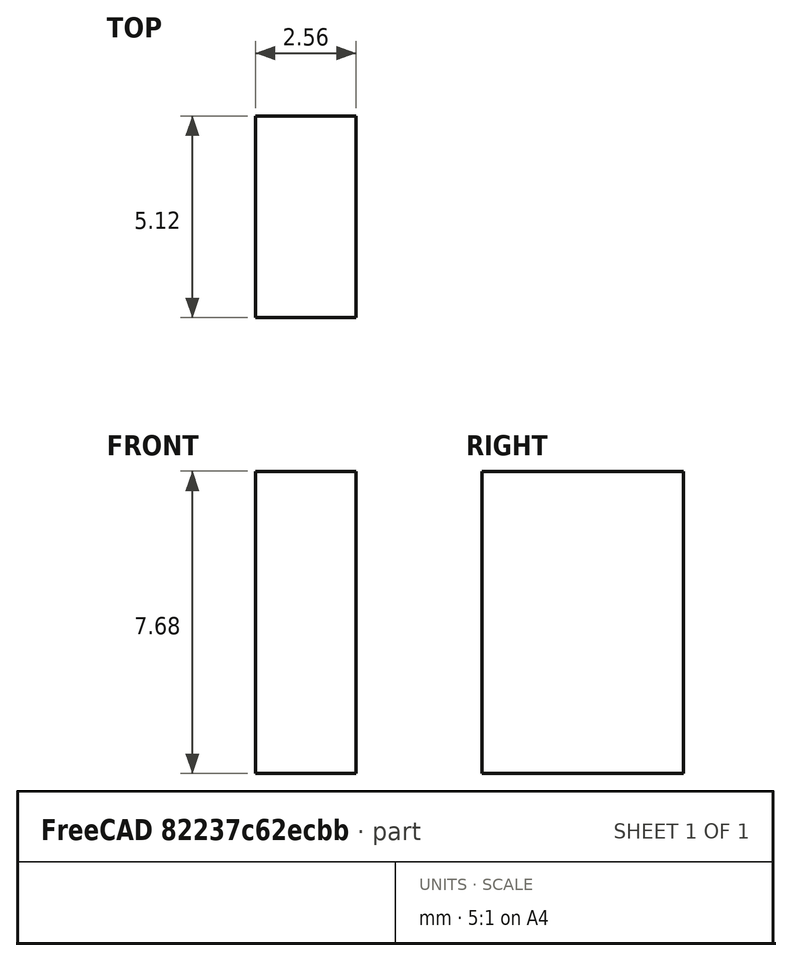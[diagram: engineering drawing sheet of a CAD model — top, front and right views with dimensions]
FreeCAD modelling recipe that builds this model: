
FCSTD DOCUMENT  (FreeCAD 0.19R)
Label: simple-ctrlr
License: All rights reserved
LicenseURL: http://en.wikipedia.org/wiki/All_rights_reserved
objects: App::FeaturePython×2, Part::Box×1, App::DocumentObjectGroupPython×1
note: 1 computed .brp shape members not serialized (recipe doc carries the construction recipe); baked Part::Feature solids carry a one-line shape summary decoded from their .brp

FEATURE [Part::Box] Box  label="Cube"
  AttacherType = Attacher::AttachEngine3D
  Height = 7.67718
  Length = 2.55906
  Width = 5.11812
  expr: .Placement.Rotation.Axis = IncommingData.DataFlow_1.Rotation.Axis
  expr: .Placement.Rotation.Angle = IncommingData.DataFlow_1.Rotation.Angle
  expr: Height = 30mm * IncommingData.DataFlow_0
  expr: Width = 20mm * IncommingData.DataFlow_0
  expr: Length = 10mm * IncommingData.DataFlow_0
FEATURE [App::FeaturePython] OutgoingData  # WARN: FeaturePython — macro-defined, semantics opaque (R4)
FEATURE [App::FeaturePython] IncommingData  # WARN: FeaturePython — macro-defined, semantics opaque (R4)
  DataFlow_0 = 0.255906
FEATURE [App::DocumentObjectGroupPython] PDControler  # scripted group (container) (typed FeaturePython)
  Group = -> [IncommingData,OutgoingData]
